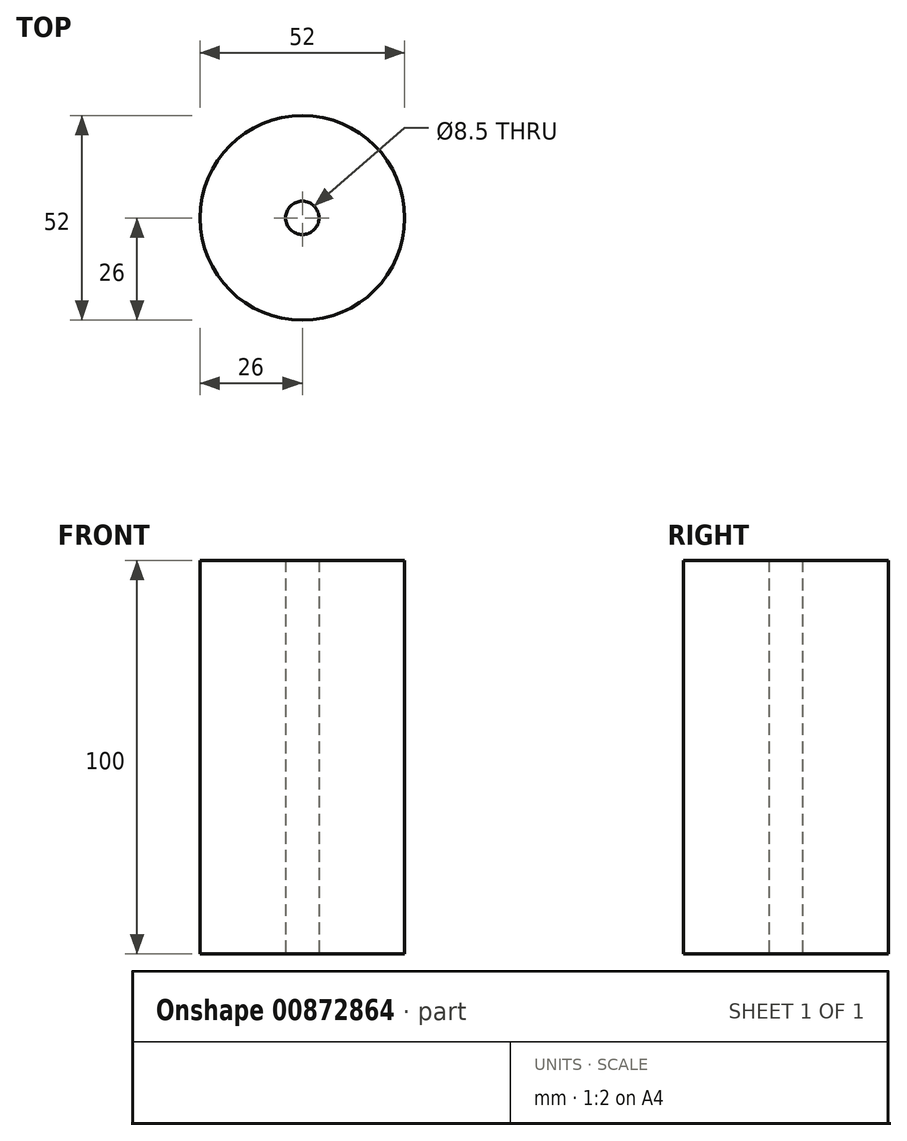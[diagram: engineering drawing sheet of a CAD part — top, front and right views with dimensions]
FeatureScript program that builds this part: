
annotation { "Feature Type Name" : "Feature", "Feature Type Description" : "" }
export const myFeature = defineFeature(function(context is Context, id is Id, definition is map)
    precondition{}
    {
        {
            var Q0;
            Q0=qCreatedBy(makeId("Top.planeOp"),FACE);
            var sketch = newSketch(context, id + "F0", { "sketchPlane" : qUnion([Q0])});
            skCircle(sketch, "E0", {"center": v(0, 0) * mm, "radius": 26 * mm});
            skCircle(sketch, "E1", {"center": v(0, 0) * mm, "radius": 4.25 * mm});
            skSolve(sketch);
        }
        {
            var Q0;
            Q0=makeQuery(id+"F0.imprint","IMPRINT",FACE,{"disambiguationData":[TD([[makeQuery(id+"F0.imprint","IMPRINT",EDGE,{"derivedFrom":sQuery(id+"F0.wireOp",EDGE,"E0")}),1.0]])]});
            var Q1;
            Q1=sQuery(id+"F0.wireOp",EDGE,"E0");
            extrude(context, id + "F1", {"entities" : qUnion([Q0]), "surfaceEntities" : qUnion([Q1]), "depth" : 100 * mm, "offsetDistance" : 25 * mm});
        }
    });
